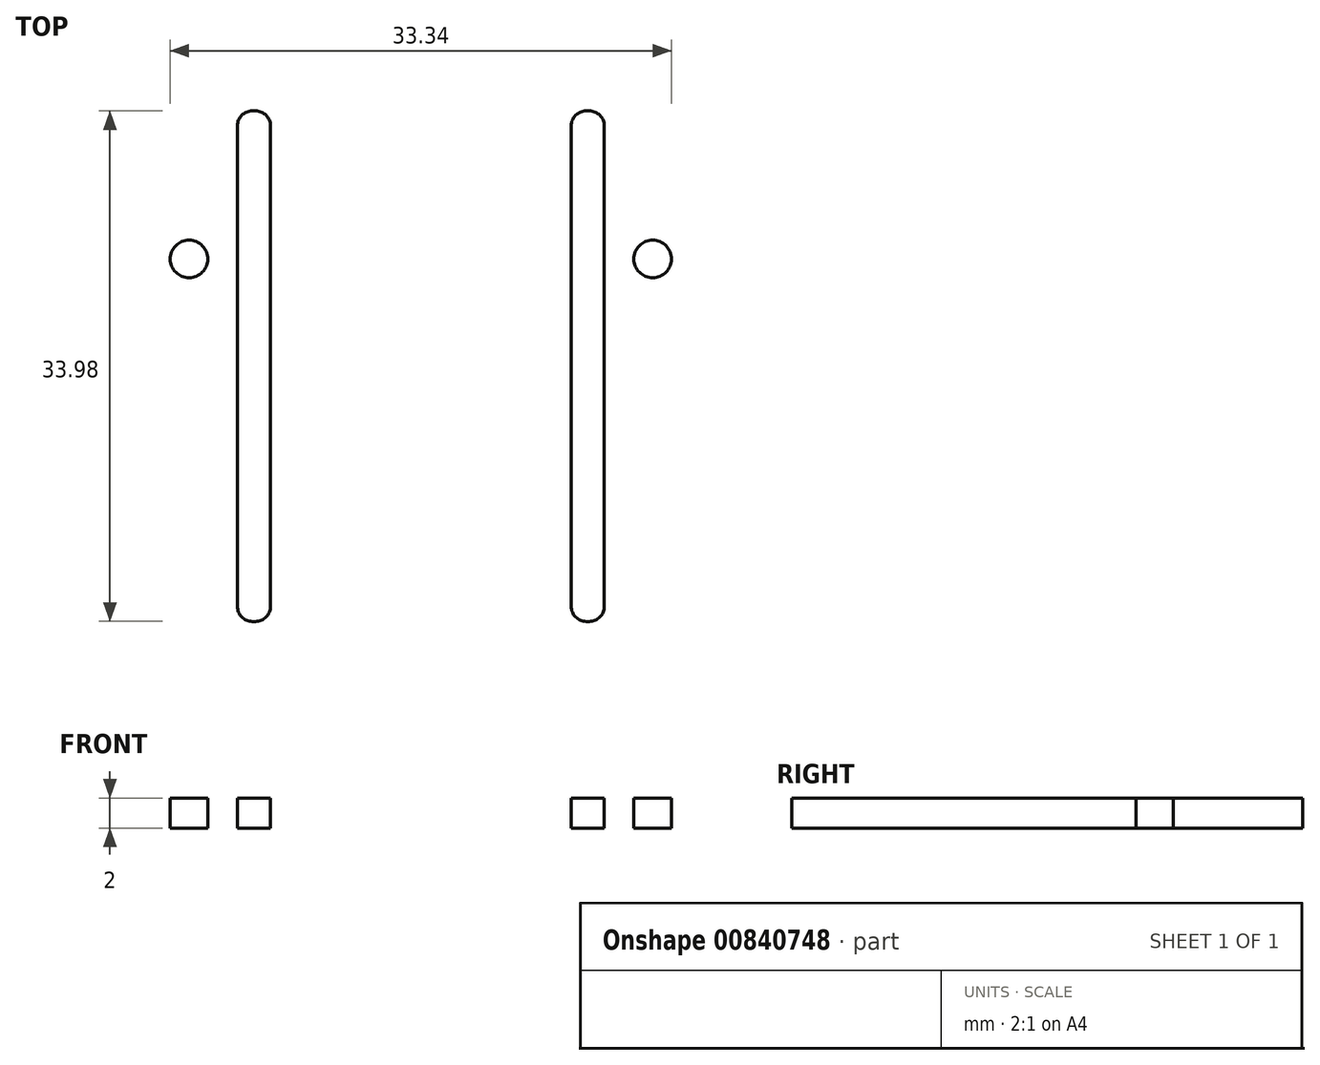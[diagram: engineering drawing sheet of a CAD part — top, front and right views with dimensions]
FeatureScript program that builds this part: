
annotation { "Feature Type Name" : "Feature", "Feature Type Description" : "" }
export const myFeature = defineFeature(function(context is Context, id is Id, definition is map)
    precondition{}
    {
        {
            var Q0;
            Q0=qCreatedBy(makeId("Top.planeOp"),FACE);
            var sketch = newSketch(context, id + "F0", { "sketchPlane" : qUnion([Q0])});
            skLineSegment(sketch, "E0", {"start": v(-17.85, -17.05) * mm, "end": v(-14.07, -26.15) * mm});
            skLineSegment(sketch, "E1.MirrorCS", {"start": v(17.85, -17.05) * mm, "end": v(14.07, -26.15) * mm});
            skArc(sketch, "E2.filletArc", {"start": v(-19, -11.3) * mm, "mid": v(-18.71, -14.23) * mm, "end": v(-17.85, -17.05) * mm});
            skArc(sketch, "E3.MirrorCS", {"start": v(19, -11.3) * mm, "mid": v(18.71, -14.23) * mm, "end": v(17.85, -17.05) * mm});
            skLineSegment(sketch, "E4", {"start": v(18.9, 41.96) * mm, "end": v(19, -11.3) * mm});
            skPoint(sketch, "E5.end.orphan", {"position": v(8.94, -30.47) * mm});
            skArc(sketch, "E6.filletArc", {"start": v(7.6, -30.47) * mm, "mid": v(11.5, -29.3) * mm, "end": v(14.07, -26.15) * mm});
            skArc(sketch, "E7.MirrorCS", {"start": v(-7.6, -30.47) * mm, "mid": v(-11.5, -29.3) * mm, "end": v(-14.07, -26.15) * mm});
            skLineSegment(sketch, "E8", {"start": v(-7.6, -30.47) * mm, "end": v(7.6, -30.47) * mm});
            skLineSegment(sketch, "E9.top", {"start": v(-3, 10.5) * mm, "end": v(3, 10.5) * mm});
            skPoint(sketch, "E10.visualSharp", {"position": v(-8, 10.5) * mm});
            skArc(sketch, "E10.filletArc", {"start": v(-8, 15.5) * mm, "mid": v(-6.54, 11.97) * mm, "end": v(-3, 10.5) * mm});
            skPoint(sketch, "E11.visualSharp", {"position": v(8, 10.5) * mm});
            skArc(sketch, "E11.filletArc", {"start": v(3, 10.5) * mm, "mid": v(6.54, 11.97) * mm, "end": v(8, 15.5) * mm});
            skLineSegment(sketch, "E12.MirrorCS", {"start": v(11, 51.62) * mm, "end": v(11.2, 51.62) * mm});
            skLineSegment(sketch, "E13.MirrorCS", {"start": v(11, 17.64) * mm, "end": v(11.2, 17.64) * mm});
            skArc(sketch, "E14.MirrorCS", {"start": v(11, 17.64) * mm, "mid": v(10.3, 17.93) * mm, "end": v(10, 18.64) * mm});
            skArc(sketch, "E15.MirrorCS", {"start": v(11.2, 51.62) * mm, "mid": v(11.9, 51.33) * mm, "end": v(12.2, 50.62) * mm});
            skArc(sketch, "E16.MirrorCS", {"start": v(12.2, 18.64) * mm, "mid": v(11.9, 17.93) * mm, "end": v(11.2, 17.64) * mm});
            skLineSegment(sketch, "E17.MirrorCS", {"start": v(11, 53.64) * mm, "end": v(11.61, 53.64) * mm});
            skArc(sketch, "E18.MirrorCS", {"start": v(10, 50.62) * mm, "mid": v(10.3, 51.33) * mm, "end": v(11, 51.62) * mm});
            skArc(sketch, "E19.MirrorCS", {"start": v(18.29, 43.82) * mm, "mid": v(18.66, 42.91) * mm, "end": v(18.9, 41.96) * mm});
            skArc(sketch, "E20.MirrorCS", {"start": v(11.61, 53.64) * mm, "mid": v(13.2, 53.19) * mm, "end": v(14.32, 51.96) * mm});
            skPoint(sketch, "E21.MirrorP", {"position": v(19, 53.66) * mm});
            skCircle(sketch, "E22.MirrorC", {"center": v(15.42, 41.76) * mm, "radius": 1.25 * mm});
            skLineSegment(sketch, "E23.MirrorCS", {"start": v(10, 18.64) * mm, "end": v(10, 50.62) * mm});
            skPoint(sketch, "E24.MirrorP", {"position": v(12.2, 17.64) * mm});
            skPoint(sketch, "E25.MirrorP", {"position": v(12.2, 51.62) * mm});
            skPoint(sketch, "E26.MirrorP", {"position": v(8, 53.63) * mm});
            skPoint(sketch, "E27.MirrorP", {"position": v(10, 17.64) * mm});
            skLineSegment(sketch, "E28.MirrorCS", {"start": v(18.29, 43.82) * mm, "end": v(14.32, 51.96) * mm});
            skPoint(sketch, "E29.MirrorP", {"position": v(10, 51.62) * mm});
            skPoint(sketch, "E30.MirrorP", {"position": v(16, 53.65) * mm});
            skPoint(sketch, "E31.MirrorP", {"position": v(13.5, 53.64) * mm});
            skLineSegment(sketch, "E32.MirrorCS", {"start": v(8, 50.64) * mm, "end": v(8, 15.5) * mm});
            skLineSegment(sketch, "E33.MirrorCS", {"start": v(12.2, 18.64) * mm, "end": v(12.2, 50.62) * mm});
            skArc(sketch, "E34.MirrorCS", {"start": v(8, 50.64) * mm, "mid": v(8.88, 52.75) * mm, "end": v(11, 53.64) * mm});
            skLineSegment(sketch, "E35.MirrorCS", {"start": v(-11, 51.62) * mm, "end": v(-11.2, 51.62) * mm});
            skArc(sketch, "E36.MirrorCS", {"start": v(-11, 17.64) * mm, "mid": v(-10.3, 17.93) * mm, "end": v(-10, 18.64) * mm});
            skArc(sketch, "E37.MirrorCS", {"start": v(-12.2, 18.64) * mm, "mid": v(-11.9, 17.93) * mm, "end": v(-11.2, 17.64) * mm});
            skArc(sketch, "E38.MirrorCS", {"start": v(-11.2, 51.62) * mm, "mid": v(-11.9, 51.33) * mm, "end": v(-12.2, 50.62) * mm});
            skLineSegment(sketch, "E39.MirrorCS", {"start": v(-11, 17.64) * mm, "end": v(-11.2, 17.64) * mm});
            skArc(sketch, "E40.MirrorCS", {"start": v(-10, 50.62) * mm, "mid": v(-10.3, 51.33) * mm, "end": v(-11, 51.62) * mm});
            skLineSegment(sketch, "E41.MirrorCS", {"start": v(-11, 53.64) * mm, "end": v(-11.61, 53.64) * mm});
            skArc(sketch, "E42.MirrorCS", {"start": v(-18.29, 43.82) * mm, "mid": v(-18.66, 42.91) * mm, "end": v(-18.9, 41.96) * mm});
            skArc(sketch, "E43.MirrorCS", {"start": v(-11.61, 53.64) * mm, "mid": v(-13.2, 53.19) * mm, "end": v(-14.32, 51.96) * mm});
            skCircle(sketch, "E44.MirrorC", {"center": v(-15.42, 41.76) * mm, "radius": 1.25 * mm});
            skArc(sketch, "E45.MirrorCS", {"start": v(-8, 50.64) * mm, "mid": v(-8.88, 52.75) * mm, "end": v(-11, 53.64) * mm});
            skLineSegment(sketch, "E46.MirrorCS", {"start": v(-10, 18.64) * mm, "end": v(-10, 50.62) * mm});
            skPoint(sketch, "E47.MirrorP", {"position": v(-10, 51.62) * mm});
            skLineSegment(sketch, "E48.MirrorCS", {"start": v(-8, 50.64) * mm, "end": v(-8, 15.5) * mm});
            skPoint(sketch, "E49.MirrorP", {"position": v(-8, 53.63) * mm});
            skPoint(sketch, "E50.MirrorP", {"position": v(-19, 53.66) * mm});
            skPoint(sketch, "E51.MirrorP", {"position": v(-13.5, 53.64) * mm});
            skPoint(sketch, "E52.MirrorP", {"position": v(-10, 17.64) * mm});
            skLineSegment(sketch, "E53.MirrorCS", {"start": v(-12.2, 18.64) * mm, "end": v(-12.2, 50.62) * mm});
            skPoint(sketch, "E54.MirrorP", {"position": v(-12.2, 17.64) * mm});
            skLineSegment(sketch, "E55.MirrorCS", {"start": v(-18.29, 43.82) * mm, "end": v(-14.32, 51.96) * mm});
            skPoint(sketch, "E56.MirrorP", {"position": v(-12.2, 51.62) * mm});
            skPoint(sketch, "E57.MirrorP", {"position": v(-16, 53.65) * mm});
            skLineSegment(sketch, "E58.MirrorCS", {"start": v(-18.9, 41.96) * mm, "end": v(-19, -11.3) * mm});
            skSolve(sketch);
        }
        {
            var Q0;
            Q0 = qSketchRegion(id + "F0", true);
            extrude(context, id + "F1", {"entities" : qUnion([Q0]), "depth" : 2 * mm, "offsetDistance" : 25 * mm});
        }
    });
